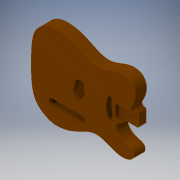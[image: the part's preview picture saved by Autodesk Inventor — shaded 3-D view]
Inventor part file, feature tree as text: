
AUTODESK INVENTOR PART (.ipt)
format: ipt  version: 2018 (Build 220112000, 112)  size: 584,192 bytes
history: native  units: in
note: dims shown in document units (in); Inventor stores cm internally (conversion verified against a paired STEP export)
features: sketch x13, other x6, projected_geometry x6, extrude x5, revolve x4, split x4, plane x2, hole x1
ambient origin geometry x8: Origin, YZ Plane, XZ Plane, XY Plane, X Axis, Y Axis, Z Axis, Center Point
bodies: Solid1 (feature_tree), body (feature_tree)
feature tree (41):
  sketch  "Sketch1"  dims[d10=14.3434in d17=7.0669in]
  extrude  "neck slot"  Depth=7.0669in
  extrude  "bridge pickup cavity"  Depth=9.3158in
  extrude  "neck pickup cavity"  Depth=0.1969in
  sketch  "Sketch11"  dims[d35=0.25in d36=3.002in]
  extrude  "control cavity"  Depth=1.6929in
  extrude  "back cavity"  Depth=0.25in
  hole  "arduino mount holes"  [1 undecoded]
  other  "Bridge Mount Screw Hole Datum"
  other  "Bridge Pickup to Control Hole Plane"
  revolve  "Revolution1"  [1 undecoded]
  other  "Bridge Pickup to Back Cavity Hole Plane"
  split  "Split1"
  revolve  "Revolution2"  [1 undecoded]
  sketch  "Sketch17"  dims[d76=0.715in]
  plane  "Work Plane6"
  split  "Split2"
  revolve  "Revolution3"  [1 undecoded]
  plane  "Work Plane7"
  split  "Split3"
  revolve  "Revolution4"  [1 undecoded]
  split  "Split4"
  other  "Image1"
  sketch  "Sketch2"  dims[d24=7.4596in d25=9.3158in]
  sketch  "Sketch3"  dims[d26=0.1969in d27=0.1969in]
  projected_geometry  "Projected Loop1"
  sketch  "Sketch6"  dims[d28=0.4331in d31=1.6929in]
  sketch  "Sketch9"  dims[d32=1.75in d33=0.0in d34=0.25in]
  projected_geometry  "Projected Loop4"
  projected_geometry  "Projected Loop5"
  sketch  "Sketch12"  dims[d37=0.625in d38=0.0in d54=0.85in d55=0.0in]
  sketch  "Sketch13"  dims[d69=2.135in d70=3.002in]
  projected_geometry  "Projected Loop7"
  sketch  "Sketch15"  dims[d72=0.343in d73=0.4315in]
  projected_geometry  "Projected Loop8"
  sketch  "Sketch16"  dims[d74=0.617in d75=2.564in]
  other  "Work Axis3"
  sketch  "Sketch18"  dims[d77=0.687in d78=0.0in]
  projected_geometry  "Projected Loop11"
  other  "Work Axis4"
  sketch  "Sketch19"  dims[d79=7.37in d80=0.265in d81=0.43in d82=2.222in d83=1.71in d84=1.577in d85=1.025in d87=0.134in d88=2.495in d89=0.982in d97=1.0in d98=4.57in d99=5.06in d100=3.125in d101=1.5in d102=0.0in d107=0.25in d108=2.3622in d109=6.2992in d110=2.1654in d111=4.9213in d112=0.9843in d113=0.0in d114=0.6982in d117=0.25in d119=6.378in d120=8.9472in d121=6.3764in d122=9.058in d123=12.7966in d125=1.9in d126=2.95in d127=3.25in d128=0.2362in d129=0.0787in d130=0.2362in d131=0.119in d132=0.0787in d133=0.5635in d134=0.1969in d135=0.8108in d137=-7.37in d138=1.71in d139=0.125in d140=0.125in d141=0.1969in d142=0.1969in d143=90.0deg d144=1.7717in d145=0.125in d146=0.125in d147=0.0787in d148=0.0787in d149=90.0deg d151=0.1969in d153=0.125in d154=0.125in d155=0.1969in d156=90.0deg d157=135.0deg d159=0.875in d160=0.875in d161=90.0deg]
note: 5 required parameter values undecoded (feature->parameter linkage not recoverable at this tier; creation-order binding heuristic only, values carry confidence <= 0.55)